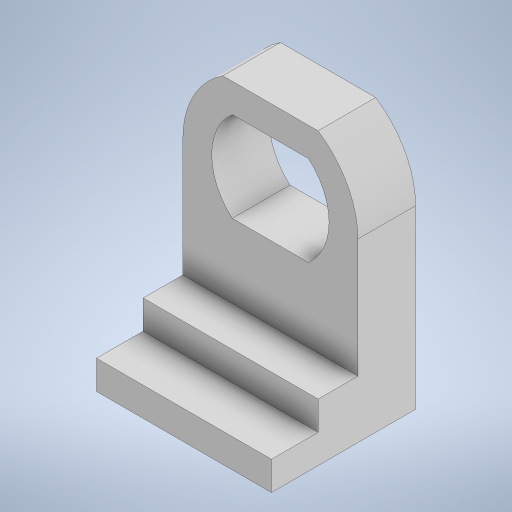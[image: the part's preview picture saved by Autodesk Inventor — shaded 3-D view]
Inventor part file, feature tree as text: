
AUTODESK INVENTOR PART (.ipt)
format: ipt  version: 2023 (Build 270158000, 158)  size: 249,344 bytes
history: native  units: mm
features: extrude x3, plane x2, sketch x1
ambient origin geometry x8: Origin, YZ Plane, XZ Plane, XY Plane, X Axis, Y Axis, Z Axis, Center Point
bodies: Solid1 (feature_tree)
feature tree (6):
  plane  "Work Plane1"
  sketch  "Sketch2"  dims[d5=0.3mm d6=5.0mm d7=30.6mm d8=5.0mm d9=5.0mm d10=10.0mm d11=0.0mm d12=10.0mm d13=0.0mm d14=6.9mm d15=0.0mm]
  extrude  "Extrusion1"  Depth=5.0mm
  plane  "Work Plane2"
  extrude  "Extrusion2"  Depth=6.9mm
  extrude  "Extrusion3"  Depth=5.0mm
